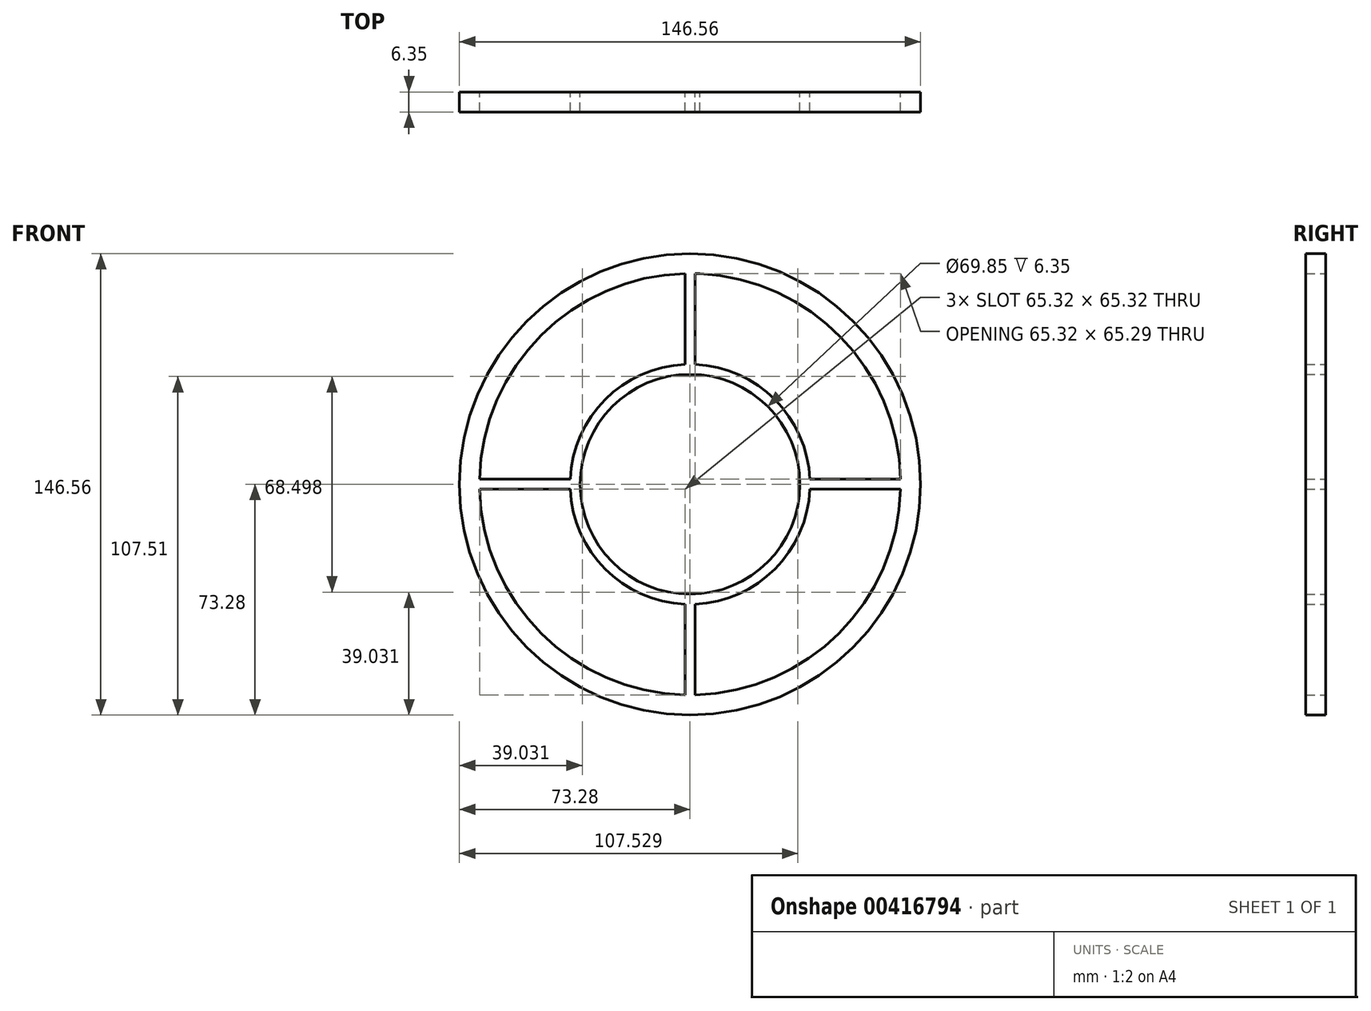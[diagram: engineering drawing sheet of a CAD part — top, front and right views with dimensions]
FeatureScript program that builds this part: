
annotation { "Feature Type Name" : "Feature", "Feature Type Description" : "" }
export const myFeature = defineFeature(function(context is Context, id is Id, definition is map)
    precondition{}
    {
        {
            var Q0;
            Q0=qCreatedBy(makeId("Front.planeOp"),FACE);
            var sketch = newSketch(context, id + "F0", { "sketchPlane" : qUnion([Q0])});
            skCircle(sketch, "E0", {"center": v(0, 0) * mm, "radius": 73.28 * mm});
            skArc(sketch, "E1.0", {"start": v(-1.59, 66.91) * mm, "mid": v(-47.33, 47.33) * mm, "end": v(-66.91, 1.59) * mm});
            skArc(sketch, "E2", {"start": v(-1.59, 38.07) * mm, "mid": v(-26.94, 26.94) * mm, "end": v(-38.07, 1.59) * mm});
            skCircle(sketch, "E3.0", {"center": v(0, 0) * mm, "radius": 34.93 * mm});
            skLineSegment(sketch, "E4.bottom", {"start": v(-66.91, 1.59) * mm, "end": v(-38.07, 1.59) * mm});
            skLineSegment(sketch, "E4.top", {"start": v(-66.91, -1.59) * mm, "end": v(-38.07, -1.59) * mm});
            skLineSegment(sketch, "E5.bottom", {"start": v(1.59, 66.87) * mm, "end": v(3.14, 66.86) * mm});
            skLineSegment(sketch, "E5.left", {"start": v(-1.59, 66.91) * mm, "end": v(-1.59, 37.97) * mm});
            skLineSegment(sketch, "E5.right", {"start": v(1.59, 66.87) * mm, "end": v(1.59, 38.07) * mm});
            skLineSegment(sketch, "E6.bottom", {"start": v(38.07, 1.59) * mm, "end": v(66.91, 1.59) * mm});
            skLineSegment(sketch, "E6.top", {"start": v(38.07, -1.59) * mm, "end": v(66.91, -1.59) * mm});
            skLineSegment(sketch, "E7.left", {"start": v(-1.59, -38.07) * mm, "end": v(-1.59, -66.91) * mm});
            skLineSegment(sketch, "E7.right", {"start": v(1.59, -38.07) * mm, "end": v(1.59, -66.91) * mm});
            skArc(sketch, "E8.trimOffspring", {"start": v(38.07, 1.59) * mm, "mid": v(26.94, 26.94) * mm, "end": v(1.59, 38.07) * mm});
            skArc(sketch, "E9.trimOffspring", {"start": v(66.91, 1.59) * mm, "mid": v(47.87, 46.77) * mm, "end": v(3.14, 66.86) * mm});
            skArc(sketch, "E10.trimOffspring", {"start": v(1.59, -66.91) * mm, "mid": v(47.33, -47.33) * mm, "end": v(66.91, -1.59) * mm});
            skArc(sketch, "E11.trimOffspring", {"start": v(1.59, -38.07) * mm, "mid": v(26.94, -26.94) * mm, "end": v(38.07, -1.59) * mm});
            skArc(sketch, "E12.trimOffspring", {"start": v(-38.07, -1.59) * mm, "mid": v(-26.94, -26.94) * mm, "end": v(-1.59, -38.07) * mm});
            skArc(sketch, "E13.trimOffspring", {"start": v(-66.91, -1.59) * mm, "mid": v(-47.33, -47.33) * mm, "end": v(-1.59, -66.91) * mm});
            skSolve(sketch);
        }
        {
            var Q0;
            {var subQ1=sQuery(id+"F0.wireOp",EDGE,"E4.bottom");Q0=makeQuery(id+"F0.imprint","IMPRINT",FACE,{"disambiguationData":[TD([[makeQuery(id+"F0.imprint","IMPRINT",EDGE,{"derivedFrom":subQ1}),-1.0]])]});}
            var Q1;
            Q1=makeQuery(id+"F0.imprint","IMPRINT",FACE,{"disambiguationData":[TD([[makeQuery(id+"F0.imprint","IMPRINT",EDGE,{"derivedFrom":sQuery(id+"F0.wireOp",EDGE,"E3.0")}),-1.0]])]});
            var Q2;
            {var subQ1=sQuery(id+"F0.wireOp",EDGE,"E6.bottom");Q2=makeQuery(id+"F0.imprint","IMPRINT",FACE,{"disambiguationData":[TD([[makeQuery(id+"F0.imprint","IMPRINT",EDGE,{"derivedFrom":subQ1}),-1.0]])]});}
            var Q3;
            Q3=makeQuery(id+"F0.imprint","IMPRINT",FACE,{"disambiguationData":[TD([[makeQuery(id+"F0.imprint","IMPRINT",EDGE,{"derivedFrom":sQuery(id+"F0.wireOp",EDGE,"E0")}),1.0]])]});
            var Q4;
            Q4=makeQuery(id+"F0.imprint","IMPRINT",FACE,{"disambiguationData":[TD([[makeQuery(id+"F0.imprint","IMPRINT",EDGE,{"derivedFrom":sQuery(id+"F0.wireOp",EDGE,"E7.top")}),1.0]])]});
            extrude(context, id + "F1", {"entities" : qUnion([Q0, Q1, Q2, Q3, Q4]), "offsetDistance" : 25.4 * mm, "depth" : 6.35 * mm});
        }
    });
